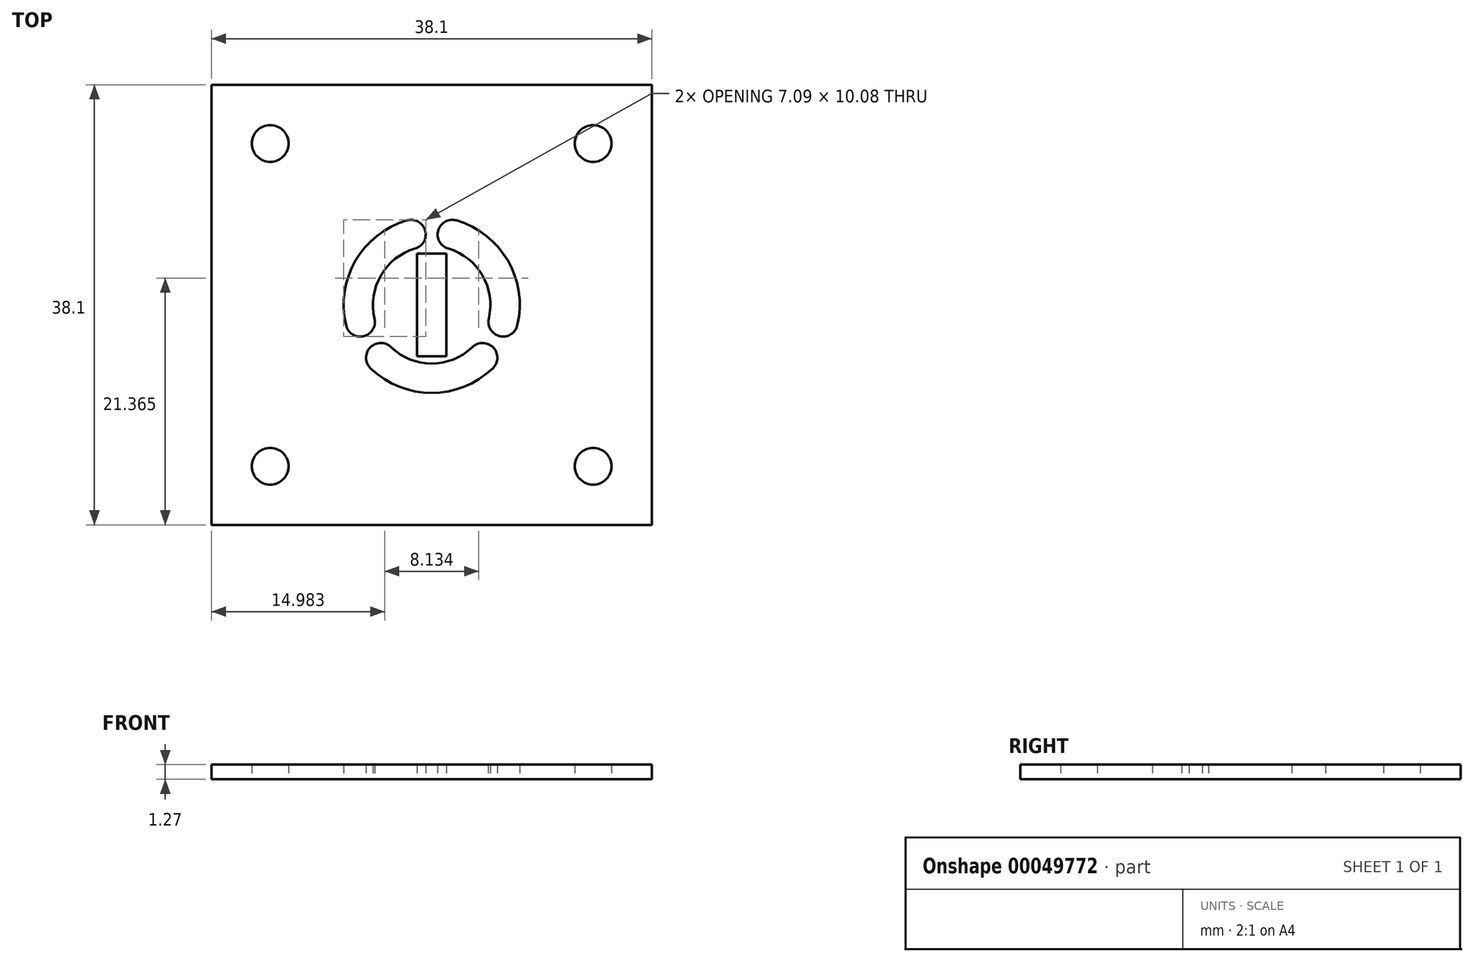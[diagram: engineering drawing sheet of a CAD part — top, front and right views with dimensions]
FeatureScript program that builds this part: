
annotation { "Feature Type Name" : "Feature", "Feature Type Description" : "" }
export const myFeature = defineFeature(function(context is Context, id is Id, definition is map)
    precondition{}
    {
        {
            var Q0;
            Q0=qCreatedBy(makeId("Top.planeOp"),FACE);
            var sketch = newSketch(context, id + "F0", { "sketchPlane" : qUnion([Q0])});
            skLineSegment(sketch, "E0.rect.bottom", {"start": v(19.05, -19.05) * mm, "end": v(-19.05, -19.05) * mm});
            skLineSegment(sketch, "E0.rect.top", {"start": v(19.05, 19.05) * mm, "end": v(-19.05, 19.05) * mm});
            skLineSegment(sketch, "E0.rect.left", {"start": v(19.05, -19.05) * mm, "end": v(19.05, 19.05) * mm});
            skLineSegment(sketch, "E0.rect.right", {"start": v(-19.05, -19.05) * mm, "end": v(-19.05, 19.05) * mm});
            skPoint(sketch, "E0.rect.middle", {"position": v(0, 0) * mm});
            skSolve(sketch);
        }
        {
            var Q0;
            Q0=qSketchRegion(id+"F0",true);
            extrude(context, id + "F1", {"entities" : qUnion([Q0]), "depth" : 1.27 * mm});
        }
        {
            var Q0;
            Q0=qCreatedBy(makeId("Top.planeOp"),FACE);
            var sketch = newSketch(context, id + "F2", { "sketchPlane" : qUnion([Q0])});
            skLineSegment(sketch, "E1", {"start": v(0.52, 6.2) * mm, "end": v(0.52, 6.2) * mm});
            skLineSegment(sketch, "E2", {"start": v(-0.52, 6.2) * mm, "end": v(-0.52, 6.2) * mm});
            skLineSegment(sketch, "E3", {"start": v(5.13, -3.52) * mm, "end": v(5.13, -3.52) * mm});
            skLineSegment(sketch, "E4", {"start": v(5.64, -2.62) * mm, "end": v(5.64, -2.62) * mm});
            skLineSegment(sketch, "E5", {"start": v(-5.64, -2.62) * mm, "end": v(-5.64, -2.62) * mm});
            skLineSegment(sketch, "E6", {"start": v(-5.13, -3.52) * mm, "end": v(-5.13, -3.52) * mm});
            skArc(sketch, "E7", {"start": v(-2.14, 7.31) * mm, "mid": v(-6.6, 3.83) * mm, "end": v(-7.41, -1.77) * mm});
            skArc(sketch, "E8", {"start": v(7.41, -1.77) * mm, "mid": v(6.6, 3.83) * mm, "end": v(2.14, 7.31) * mm});
            skArc(sketch, "E9", {"start": v(-5.29, -5.49) * mm, "mid": v(0, -7.62) * mm, "end": v(5.29, -5.49) * mm});
            skArc(sketch, "E10", {"start": v(-1.43, 4.88) * mm, "mid": v(-4.4, 2.55) * mm, "end": v(-4.94, -1.18) * mm});
            skArc(sketch, "E11", {"start": v(4.94, -1.18) * mm, "mid": v(4.4, 2.55) * mm, "end": v(1.43, 4.88) * mm});
            skArc(sketch, "E12", {"start": v(-3.53, -3.66) * mm, "mid": v(0, -5.08) * mm, "end": v(3.53, -3.66) * mm});
            skPoint(sketch, "E13.visualSharp", {"position": v(-6.9, -3.21) * mm});
            skArc(sketch, "E13.filletArc", {"start": v(-7.41, -1.77) * mm, "mid": v(-6.73, -2.62) * mm, "end": v(-5.64, -2.62) * mm});
            skPoint(sketch, "E14.visualSharp", {"position": v(-4.6, -2.14) * mm});
            skArc(sketch, "E14.filletArc", {"start": v(-5.64, -2.62) * mm, "mid": v(-5.03, -2.03) * mm, "end": v(-4.94, -1.18) * mm});
            skPoint(sketch, "E15.visualSharp", {"position": v(-0.64, 7.6) * mm});
            skArc(sketch, "E15.filletArc", {"start": v(-0.52, 6.2) * mm, "mid": v(-1.07, 7.14) * mm, "end": v(-2.14, 7.31) * mm});
            skPoint(sketch, "E16.visualSharp", {"position": v(-0.42, 5.06) * mm});
            skArc(sketch, "E16.filletArc", {"start": v(-1.43, 4.88) * mm, "mid": v(-0.74, 5.38) * mm, "end": v(-0.52, 6.2) * mm});
            skPoint(sketch, "E17.visualSharp", {"position": v(0.42, 5.06) * mm});
            skArc(sketch, "E17.filletArc", {"start": v(0.52, 6.2) * mm, "mid": v(0.74, 5.38) * mm, "end": v(1.43, 4.88) * mm});
            skPoint(sketch, "E18.visualSharp", {"position": v(0.64, 7.6) * mm});
            skArc(sketch, "E18.filletArc", {"start": v(2.14, 7.31) * mm, "mid": v(1.07, 7.14) * mm, "end": v(0.52, 6.2) * mm});
            skPoint(sketch, "E19.visualSharp", {"position": v(4.6, -2.14) * mm});
            skArc(sketch, "E19.filletArc", {"start": v(4.94, -1.18) * mm, "mid": v(5.03, -2.03) * mm, "end": v(5.64, -2.62) * mm});
            skPoint(sketch, "E20.visualSharp", {"position": v(6.9, -3.21) * mm});
            skArc(sketch, "E20.filletArc", {"start": v(5.64, -2.62) * mm, "mid": v(6.73, -2.62) * mm, "end": v(7.41, -1.77) * mm});
            skPoint(sketch, "E21.visualSharp", {"position": v(4.19, -2.88) * mm});
            skArc(sketch, "E21.filletArc", {"start": v(5.13, -3.52) * mm, "mid": v(4.3, -3.3) * mm, "end": v(3.53, -3.66) * mm});
            skPoint(sketch, "E22.visualSharp", {"position": v(6.28, -4.32) * mm});
            skArc(sketch, "E22.filletArc", {"start": v(5.29, -5.49) * mm, "mid": v(5.67, -4.47) * mm, "end": v(5.13, -3.52) * mm});
            skPoint(sketch, "E23.visualSharp", {"position": v(-6.28, -4.32) * mm});
            skArc(sketch, "E23.filletArc", {"start": v(-5.13, -3.52) * mm, "mid": v(-5.67, -4.47) * mm, "end": v(-5.29, -5.49) * mm});
            skPoint(sketch, "E24.visualSharp", {"position": v(-4.19, -2.88) * mm});
            skArc(sketch, "E24.filletArc", {"start": v(-3.53, -3.66) * mm, "mid": v(-4.3, -3.3) * mm, "end": v(-5.13, -3.52) * mm});
            skSolve(sketch);
        }
        {
            var Q0;
            Q0=qSketchRegion(id+"F2",true);
            extrude(context, id + "F3", {"entities" : qUnion([Q0]), "operationType" : NewBodyOperationType.REMOVE, "depth" : 25.4 * mm});
        }
        {
            var Q0;
            Q0=qCreatedBy(makeId("Top.planeOp"),FACE);
            var sketch = newSketch(context, id + "F4", { "sketchPlane" : qUnion([Q0])});
            skCircle(sketch, "E25", {"center": v(13.97, 13.97) * mm, "radius": 1.59 * mm});
            skCircle(sketch, "E26", {"center": v(13.97, -13.97) * mm, "radius": 1.59 * mm});
            skCircle(sketch, "E27", {"center": v(-13.97, -13.97) * mm, "radius": 1.59 * mm});
            skCircle(sketch, "E28", {"center": v(-13.97, 13.97) * mm, "radius": 1.59 * mm});
            skLineSegment(sketch, "E29.bottom", {"start": v(-1.27, 4.45) * mm, "end": v(1.27, 4.45) * mm});
            skLineSegment(sketch, "E29.top", {"start": v(-1.27, -4.45) * mm, "end": v(1.27, -4.45) * mm});
            skLineSegment(sketch, "E29.left", {"start": v(-1.27, 4.45) * mm, "end": v(-1.27, -4.45) * mm});
            skLineSegment(sketch, "E29.right", {"start": v(1.27, 4.45) * mm, "end": v(1.27, -4.45) * mm});
            skPoint(sketch, "E29.middle", {"position": v(0, 0) * mm});
            skSolve(sketch);
        }
        {
            var Q0;
            Q0=qSketchRegion(id+"F4",true);
            extrude(context, id + "F5", {"entities" : qUnion([Q0]), "operationType" : NewBodyOperationType.REMOVE, "depth" : 25.4 * mm});
        }
    });
